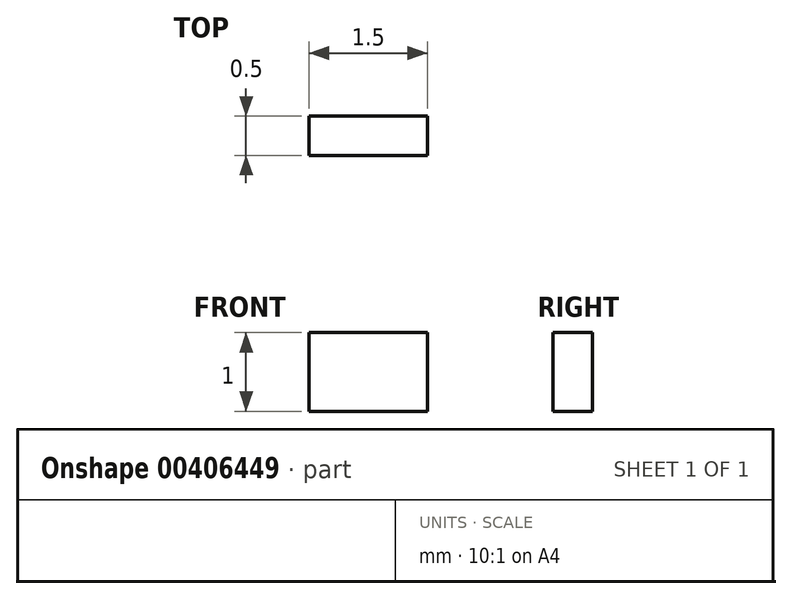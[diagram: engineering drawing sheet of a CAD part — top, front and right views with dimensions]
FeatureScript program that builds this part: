
annotation { "Feature Type Name" : "Feature", "Feature Type Description" : "" }
export const myFeature = defineFeature(function(context is Context, id is Id, definition is map)
    precondition{}
    {
        {
            var Q0;
            Q0=qCreatedBy(makeId("Top.planeOp"),FACE);
            var sketch = newSketch(context, id + "F0", { "sketchPlane" : qUnion([Q0])});
            skLineSegment(sketch, "E0.bottom", {"start": v(0, 0) * mm, "end": v(1.5, 0) * mm});
            skLineSegment(sketch, "E0.top", {"start": v(0, 0.5) * mm, "end": v(1.5, 0.5) * mm});
            skLineSegment(sketch, "E0.left", {"start": v(0, 0) * mm, "end": v(0, 0.5) * mm});
            skLineSegment(sketch, "E0.right", {"start": v(1.5, 0) * mm, "end": v(1.5, 0.5) * mm});
            skSolve(sketch);
        }
        {
            var Q0;
            Q0=makeQuery(id+"F0.imprint","IMPRINT",FACE,{"disambiguationData":[TD([[makeQuery(id+"F0.imprint","IMPRINT",EDGE,{"derivedFrom":sQuery(id+"F0.wireOp",EDGE,"E0.bottom")}),1.0]])]});
            extrude(context, id + "F1", {"entities" : qUnion([Q0]), "depth" : 1 * mm});
        }
    });
